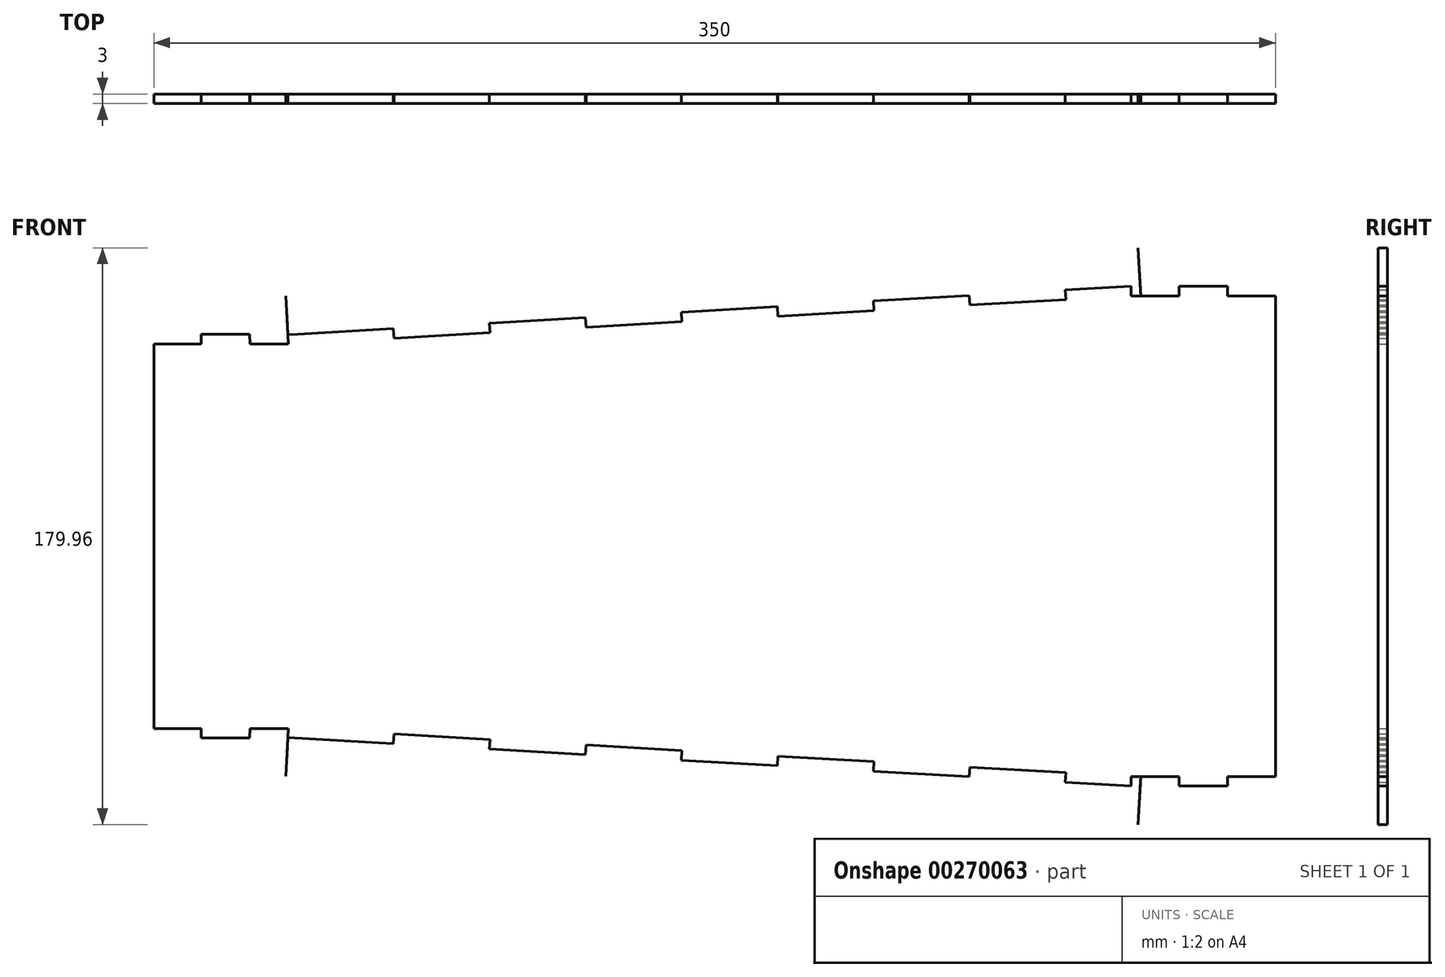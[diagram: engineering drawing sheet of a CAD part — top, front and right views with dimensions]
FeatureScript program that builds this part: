
annotation { "Feature Type Name" : "Feature", "Feature Type Description" : "" }
export const myFeature = defineFeature(function(context is Context, id is Id, definition is map)
    precondition{}
    {
        {
            var Q0;
            Q0=qCreatedBy(makeId("Front.planeOp"),FACE);
            var sketch = newSketch(context, id + "F0", { "sketchPlane" : qUnion([Q0])});
            skLineSegment(sketch, "E0", {"start": v(0, 0) * mm, "end": v(-130, 0) * mm, "construction": true});
            skLineSegment(sketch, "E1", {"start": v(0, 0) * mm, "end": v(130, 0) * mm, "construction": true});
            skLineSegment(sketch, "E2", {"start": v(130, 0) * mm, "end": v(130, 75) * mm, "construction": true});
            skLineSegment(sketch, "E3", {"start": v(-130, 0) * mm, "end": v(-130, 60) * mm, "construction": true});
            skLineSegment(sketch, "E4", {"start": v(-130, 60) * mm, "end": v(130, 75) * mm, "construction": true});
            skLineSegment(sketch, "E5.0", {"start": v(-133, 0) * mm, "end": v(-133, 60) * mm, "construction": true});
            skLineSegment(sketch, "E6.0", {"start": v(133, 0) * mm, "end": v(133, 75) * mm, "construction": true});
            skLineSegment(sketch, "E7", {"start": v(-100.22, 64.73) * mm, "end": v(-130.17, 63) * mm});
            skLineSegment(sketch, "E8", {"start": v(-100.22, 64.73) * mm, "end": v(-100.05, 61.73) * mm});
            skLineSegment(sketch, "E9", {"start": v(-100.05, 61.73) * mm, "end": v(-70.1, 63.46) * mm});
            skLineSegment(sketch, "E10", {"start": v(-70.1, 63.46) * mm, "end": v(-70.27, 66.45) * mm});
            skLineSegment(sketch, "E11", {"start": v(-70.27, 66.45) * mm, "end": v(-40.32, 68.18) * mm});
            skLineSegment(sketch, "E12", {"start": v(-40.32, 68.18) * mm, "end": v(-40.15, 65.18) * mm});
            skLineSegment(sketch, "E13", {"start": v(-40.15, 65.18) * mm, "end": v(-10.2, 66.91) * mm});
            skLineSegment(sketch, "E14", {"start": v(-10.2, 66.91) * mm, "end": v(-10.37, 69.9) * mm});
            skLineSegment(sketch, "E15", {"start": v(-10.37, 69.9) * mm, "end": v(19.58, 71.63) * mm});
            skLineSegment(sketch, "E16", {"start": v(19.58, 71.63) * mm, "end": v(19.75, 68.64) * mm});
            skLineSegment(sketch, "E17", {"start": v(19.75, 68.64) * mm, "end": v(49.7, 70.37) * mm});
            skLineSegment(sketch, "E18", {"start": v(49.7, 70.37) * mm, "end": v(49.53, 73.36) * mm});
            skLineSegment(sketch, "E19", {"start": v(49.53, 73.36) * mm, "end": v(79.48, 75.1) * mm});
            skLineSegment(sketch, "E20", {"start": v(79.48, 75.1) * mm, "end": v(79.65, 72.1) * mm});
            skLineSegment(sketch, "E21", {"start": v(79.65, 72.1) * mm, "end": v(109.6, 73.82) * mm});
            skLineSegment(sketch, "E22", {"start": v(130, 75) * mm, "end": v(129.92, 76.4) * mm});
            skLineSegment(sketch, "E23.0", {"start": v(-131.73, 89.95) * mm, "end": v(128.27, 104.95) * mm});
            skLineSegment(sketch, "E24", {"start": v(129.15, 89.8) * mm, "end": v(128.28, 104.78) * mm});
            skLineSegment(sketch, "E25", {"start": v(-131.74, 90.13) * mm, "end": v(-130.88, 75.15) * mm});
            skLineSegment(sketch, "E26", {"start": v(-130, 0) * mm, "end": v(-133, 0) * mm});
            skLineSegment(sketch, "E27", {"start": v(-133, 0) * mm, "end": v(-133, 30) * mm});
            skLineSegment(sketch, "E28", {"start": v(-133, 30) * mm, "end": v(-130, 30) * mm});
            skLineSegment(sketch, "E29", {"start": v(-130, 30) * mm, "end": v(-130, 60) * mm});
            skLineSegment(sketch, "E30", {"start": v(130, 0) * mm, "end": v(133, 0) * mm});
            skLineSegment(sketch, "E31", {"start": v(133, 0) * mm, "end": v(133, 30) * mm});
            skLineSegment(sketch, "E32", {"start": v(133, 30) * mm, "end": v(130, 30) * mm});
            skLineSegment(sketch, "E33", {"start": v(130, 30) * mm, "end": v(130, 60) * mm});
            skLineSegment(sketch, "E34", {"start": v(130, 60) * mm, "end": v(133, 60) * mm});
            skLineSegment(sketch, "E35", {"start": v(133, 60) * mm, "end": v(133, 75) * mm});
            skLineSegment(sketch, "E36", {"start": v(130, 75) * mm, "end": v(133, 75) * mm});
            skLineSegment(sketch, "E37.0", {"start": v(175, 0) * mm, "end": v(175, 75) * mm});
            skLineSegment(sketch, "E38.0", {"start": v(-175, 0) * mm, "end": v(-175, 60) * mm});
            skLineSegment(sketch, "E39", {"start": v(-175, 60) * mm, "end": v(-160.17, 60) * mm});
            skLineSegment(sketch, "E40", {"start": v(-130, 60) * mm, "end": v(-145, 60) * mm});
            skLineSegment(sketch, "E41", {"start": v(-145, 60) * mm, "end": v(-145.17, 63) * mm});
            skLineSegment(sketch, "E42", {"start": v(-145.17, 63) * mm, "end": v(-160.17, 63) * mm});
            skLineSegment(sketch, "E43", {"start": v(-160.17, 63) * mm, "end": v(-160.17, 60) * mm});
            skLineSegment(sketch, "E44.trimOffspring", {"start": v(-145, 60) * mm, "end": v(-130, 60) * mm});
            skLineSegment(sketch, "E45", {"start": v(-133.34, 65.75) * mm, "end": v(-133, 60) * mm});
            skLineSegment(sketch, "E46", {"start": v(-133, 60) * mm, "end": v(-133.87, 74.97) * mm});
            skLineSegment(sketch, "E47", {"start": v(-133.87, 74.97) * mm, "end": v(-130.88, 75.15) * mm});
            skLineSegment(sketch, "E48", {"start": v(-130.88, 75.15) * mm, "end": v(-131.74, 90.13) * mm});
            skLineSegment(sketch, "E49.trimOffspring", {"start": v(-133.87, 74.97) * mm, "end": v(-133.34, 65.75) * mm});
            skLineSegment(sketch, "E50.0", {"start": v(132.91, 76.58) * mm, "end": v(132.14, 89.98) * mm});
            skLineSegment(sketch, "E51", {"start": v(133, 75) * mm, "end": v(132.91, 76.58) * mm});
            skLineSegment(sketch, "E52", {"start": v(133, 75) * mm, "end": v(132.14, 89.98) * mm});
            skLineSegment(sketch, "E53", {"start": v(132.14, 89.98) * mm, "end": v(129.15, 89.8) * mm});
            skLineSegment(sketch, "E54", {"start": v(133, 75) * mm, "end": v(145, 75) * mm});
            skLineSegment(sketch, "E55", {"start": v(130, 75) * mm, "end": v(145, 75) * mm});
            skLineSegment(sketch, "E56", {"start": v(145, 75) * mm, "end": v(145, 78) * mm});
            skLineSegment(sketch, "E57", {"start": v(145, 78) * mm, "end": v(160, 78) * mm});
            skLineSegment(sketch, "E58", {"start": v(160, 78) * mm, "end": v(160, 75) * mm});
            skLineSegment(sketch, "E59", {"start": v(160, 75) * mm, "end": v(175, 75) * mm});
            skLineSegment(sketch, "E60", {"start": v(-175, 0) * mm, "end": v(175, 0) * mm, "construction": true});
            skLineSegment(sketch, "E61.MirrorCS", {"start": v(133, -75) * mm, "end": v(132.91, -76.58) * mm});
            skLineSegment(sketch, "E62.MirrorCS", {"start": v(130, -75) * mm, "end": v(129.92, -76.4) * mm});
            skLineSegment(sketch, "E63.MirrorCS", {"start": v(130, -75) * mm, "end": v(133, -75) * mm});
            skLineSegment(sketch, "E64.MirrorCS", {"start": v(-133.34, -65.75) * mm, "end": v(-133, -60) * mm});
            skLineSegment(sketch, "E65.MirrorCS", {"start": v(-133.87, -74.97) * mm, "end": v(-130.88, -75.15) * mm});
            skLineSegment(sketch, "E66.MirrorCS", {"start": v(-130, -60) * mm, "end": v(-145, -60) * mm});
            skLineSegment(sketch, "E67.MirrorCS", {"start": v(-133.87, -74.97) * mm, "end": v(-133.34, -65.75) * mm});
            skLineSegment(sketch, "E68.MirrorCS", {"start": v(129.15, -89.8) * mm, "end": v(128.28, -104.78) * mm});
            skLineSegment(sketch, "E69.MirrorCS", {"start": v(-133, -60) * mm, "end": v(-133.87, -74.97) * mm});
            skLineSegment(sketch, "E70.MirrorCS", {"start": v(-145, -60) * mm, "end": v(-130, -60) * mm});
            skLineSegment(sketch, "E71.MirrorCS", {"start": v(-130.88, -75.15) * mm, "end": v(-131.74, -90.13) * mm});
            skLineSegment(sketch, "E72.MirrorCS", {"start": v(132.14, -89.98) * mm, "end": v(129.15, -89.8) * mm});
            skLineSegment(sketch, "E73.MirrorCS", {"start": v(-145, -60) * mm, "end": v(-145.17, -63) * mm});
            skLineSegment(sketch, "E74.MirrorCS", {"start": v(133, -75) * mm, "end": v(132.14, -89.98) * mm});
            skLineSegment(sketch, "E75.MirrorCS", {"start": v(133, -75) * mm, "end": v(145, -75) * mm});
            skLineSegment(sketch, "E76.MirrorCS", {"start": v(160, -75) * mm, "end": v(175, -75) * mm});
            skLineSegment(sketch, "E77.MirrorCS", {"start": v(132.91, -76.58) * mm, "end": v(132.14, -89.98) * mm});
            skLineSegment(sketch, "E78.MirrorCS", {"start": v(160, -78) * mm, "end": v(160, -75) * mm});
            skLineSegment(sketch, "E79.MirrorCS", {"start": v(130, -75) * mm, "end": v(145, -75) * mm});
            skLineSegment(sketch, "E80.MirrorCS", {"start": v(-131.74, -90.13) * mm, "end": v(-130.88, -75.15) * mm});
            skLineSegment(sketch, "E81.MirrorCS", {"start": v(-160.17, -63) * mm, "end": v(-160.17, -60) * mm});
            skLineSegment(sketch, "E82.MirrorCS", {"start": v(145, -75) * mm, "end": v(145, -78) * mm});
            skLineSegment(sketch, "E83.MirrorCS", {"start": v(-175, -60) * mm, "end": v(-160.17, -60) * mm});
            skLineSegment(sketch, "E84.MirrorCS", {"start": v(49.7, -70.37) * mm, "end": v(49.53, -73.36) * mm});
            skLineSegment(sketch, "E85.MirrorCS", {"start": v(133, -30) * mm, "end": v(130, -30) * mm});
            skLineSegment(sketch, "E86.MirrorCS", {"start": v(-40.32, -68.18) * mm, "end": v(-40.15, -65.18) * mm});
            skLineSegment(sketch, "E87.MirrorCS", {"start": v(-133, -30) * mm, "end": v(-130, -30) * mm});
            skLineSegment(sketch, "E88.MirrorCS", {"start": v(133, -60) * mm, "end": v(133, -75) * mm});
            skLineSegment(sketch, "E89.MirrorCS", {"start": v(145, -78) * mm, "end": v(160, -78) * mm});
            skLineSegment(sketch, "E90.MirrorCS", {"start": v(-10.2, -66.91) * mm, "end": v(-10.37, -69.9) * mm});
            skLineSegment(sketch, "E91.MirrorCS", {"start": v(-145.17, -63) * mm, "end": v(-160.17, -63) * mm});
            skLineSegment(sketch, "E92.MirrorCS", {"start": v(130, -60) * mm, "end": v(133, -60) * mm});
            skLineSegment(sketch, "E93.MirrorCS", {"start": v(19.58, -71.63) * mm, "end": v(19.75, -68.64) * mm});
            skLineSegment(sketch, "E94.MirrorCS", {"start": v(79.48, -75.1) * mm, "end": v(79.65, -72.1) * mm});
            skLineSegment(sketch, "E95.MirrorCS", {"start": v(-70.1, -63.46) * mm, "end": v(-70.27, -66.45) * mm});
            skLineSegment(sketch, "E96.MirrorCS", {"start": v(-100.22, -64.73) * mm, "end": v(-100.05, -61.73) * mm});
            skLineSegment(sketch, "E97.MirrorCS", {"start": v(133, 0) * mm, "end": v(133, -30) * mm});
            skLineSegment(sketch, "E98.MirrorCS", {"start": v(19.75, -68.64) * mm, "end": v(49.7, -70.37) * mm});
            skLineSegment(sketch, "E99.MirrorCS", {"start": v(79.65, -72.1) * mm, "end": v(109.6, -73.82) * mm});
            skLineSegment(sketch, "E100.MirrorCS", {"start": v(-40.15, -65.18) * mm, "end": v(-10.2, -66.91) * mm});
            skLineSegment(sketch, "E101.MirrorCS", {"start": v(130, 0) * mm, "end": v(130, -75) * mm, "construction": true});
            skLineSegment(sketch, "E102.MirrorCS", {"start": v(130, -30) * mm, "end": v(130, -60) * mm});
            skLineSegment(sketch, "E103.MirrorCS", {"start": v(-10.37, -69.9) * mm, "end": v(19.58, -71.63) * mm});
            skLineSegment(sketch, "E104.MirrorCS", {"start": v(49.53, -73.36) * mm, "end": v(79.48, -75.1) * mm});
            skLineSegment(sketch, "E105.MirrorCS", {"start": v(-70.27, -66.45) * mm, "end": v(-40.32, -68.18) * mm});
            skLineSegment(sketch, "E106.MirrorCS", {"start": v(-100.22, -64.73) * mm, "end": v(-133.17, -62.83) * mm});
            skLineSegment(sketch, "E107.MirrorCS", {"start": v(-133, 0) * mm, "end": v(-133, -30) * mm});
            skLineSegment(sketch, "E108.MirrorCS", {"start": v(-100.05, -61.73) * mm, "end": v(-70.1, -63.46) * mm});
            skLineSegment(sketch, "E109.MirrorCS", {"start": v(-131.73, -89.95) * mm, "end": v(128.27, -104.95) * mm});
            skLineSegment(sketch, "E110.MirrorCS", {"start": v(-175, 0) * mm, "end": v(-175, -60) * mm});
            skLineSegment(sketch, "E111.MirrorCS", {"start": v(-130, -30) * mm, "end": v(-130, -60) * mm});
            skLineSegment(sketch, "E112.MirrorCS", {"start": v(-130, -60) * mm, "end": v(130, -75) * mm, "construction": true});
            skLineSegment(sketch, "E113.MirrorCS", {"start": v(-133, 0) * mm, "end": v(-133, -60) * mm, "construction": true});
            skLineSegment(sketch, "E114.MirrorCS", {"start": v(-130, 0) * mm, "end": v(-130, -60) * mm, "construction": true});
            skLineSegment(sketch, "E115.MirrorCS", {"start": v(133, 0) * mm, "end": v(133, -75) * mm, "construction": true});
            skLineSegment(sketch, "E116.MirrorCS", {"start": v(175, 0) * mm, "end": v(175, -75) * mm});
            skPoint(sketch, "E117.orphan", {"position": v(-131.73, -89.95) * mm});
            skLineSegment(sketch, "E118", {"start": v(109.6, 73.82) * mm, "end": v(109.43, 76.82) * mm});
            skLineSegment(sketch, "E119", {"start": v(109.43, 76.82) * mm, "end": v(130.02, 78) * mm});
            skLineSegment(sketch, "E120", {"start": v(130.02, 78) * mm, "end": v(130, 75) * mm});
            skLineSegment(sketch, "E121", {"start": v(109.6, -73.82) * mm, "end": v(109.43, -76.82) * mm});
            skLineSegment(sketch, "E122", {"start": v(109.43, -76.82) * mm, "end": v(129.92, -78) * mm});
            skLineSegment(sketch, "E123", {"start": v(129.92, -78) * mm, "end": v(130, -75) * mm});
            skLineSegment(sketch, "E124", {"start": v(-130.17, 63) * mm, "end": v(-133.16, 62.83) * mm});
            skSolve(sketch);
        }
        {
            var Q0;
            Q0 = qSketchRegion(id + "F0", true);
            extrude(context, id + "F1", {"entities" : qUnion([Q0]), "depth" : 3 * mm, "offsetDistance" : 25 * mm});
        }
    });
